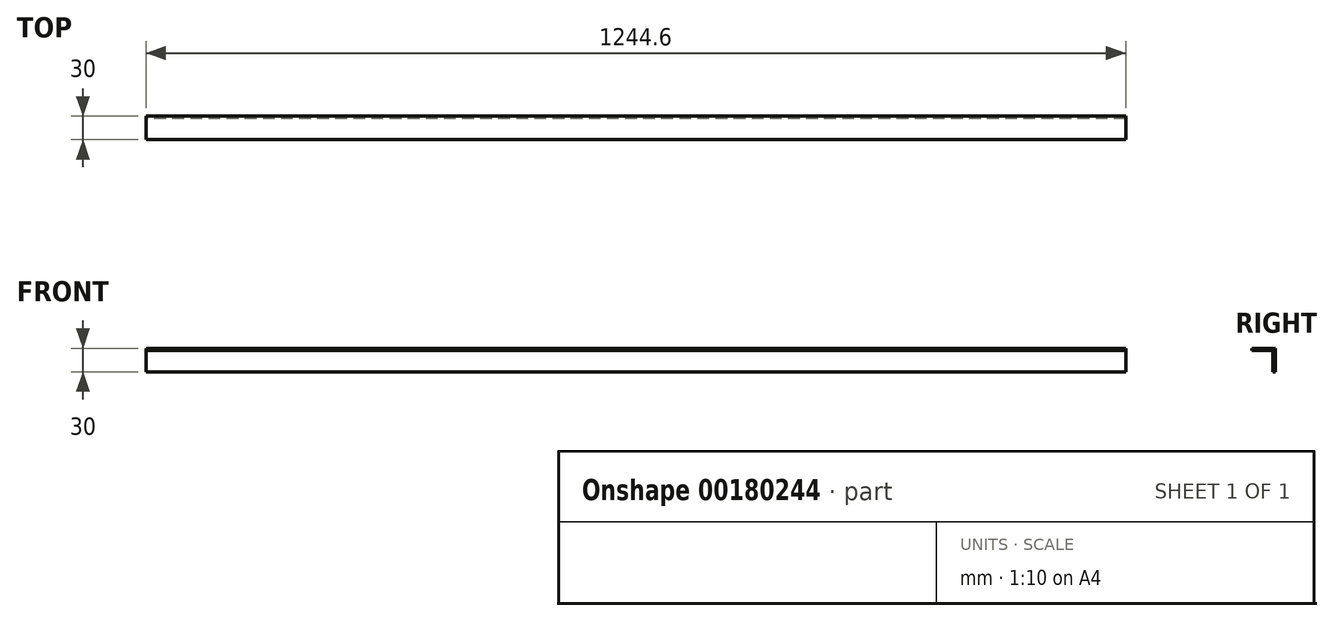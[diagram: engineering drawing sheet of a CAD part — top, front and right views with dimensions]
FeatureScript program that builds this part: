
annotation { "Feature Type Name" : "Feature", "Feature Type Description" : "" }
export const myFeature = defineFeature(function(context is Context, id is Id, definition is map)
    precondition{}
    {
        {
            var Q0;
            Q0=qCreatedBy(makeId("Right.planeOp"),FACE);
            var sketch = newSketch(context, id + "F0", { "sketchPlane" : qUnion([Q0])});
            skLineSegment(sketch, "E0", {"start": v(0, 0) * mm, "end": v(-30, 0) * mm});
            skLineSegment(sketch, "E1.filletArc", {"start": v(-3, 3) * mm, "end": v(-3, 3) * mm});
            skLineSegment(sketch, "E2.MirrorCS", {"start": v(-3, -30) * mm, "end": v(0, -30) * mm});
            skLineSegment(sketch, "E3.MirrorCS", {"start": v(-30, 0) * mm, "end": v(-30, -3) * mm});
            skLineSegment(sketch, "E4.MirrorCS", {"start": v(-3, -3) * mm, "end": v(-3, -3) * mm});
            skLineSegment(sketch, "E5.MirrorCS", {"start": v(-3, -3) * mm, "end": v(-3, -30) * mm});
            skLineSegment(sketch, "E6.MirrorCS", {"start": v(-3, -3) * mm, "end": v(-30, -3) * mm});
            skLineSegment(sketch, "E7.MirrorCS", {"start": v(0, 0) * mm, "end": v(0, -30) * mm});
            skSolve(sketch);
        }
        {
            var Q0;
            Q0=makeQuery(id+"F0.imprint","IMPRINT",FACE,{"disambiguationData":[TD([[makeQuery(id+"F0.imprint","IMPRINT",EDGE,{"derivedFrom":sQuery(id+"F0.wireOp",EDGE,"E2.MirrorCS")}),1.0]])]});
            extrude(context, id + "F1", {"entities" : qUnion([Q0]), "depth" : 1244.6 * mm});
        }
    });
